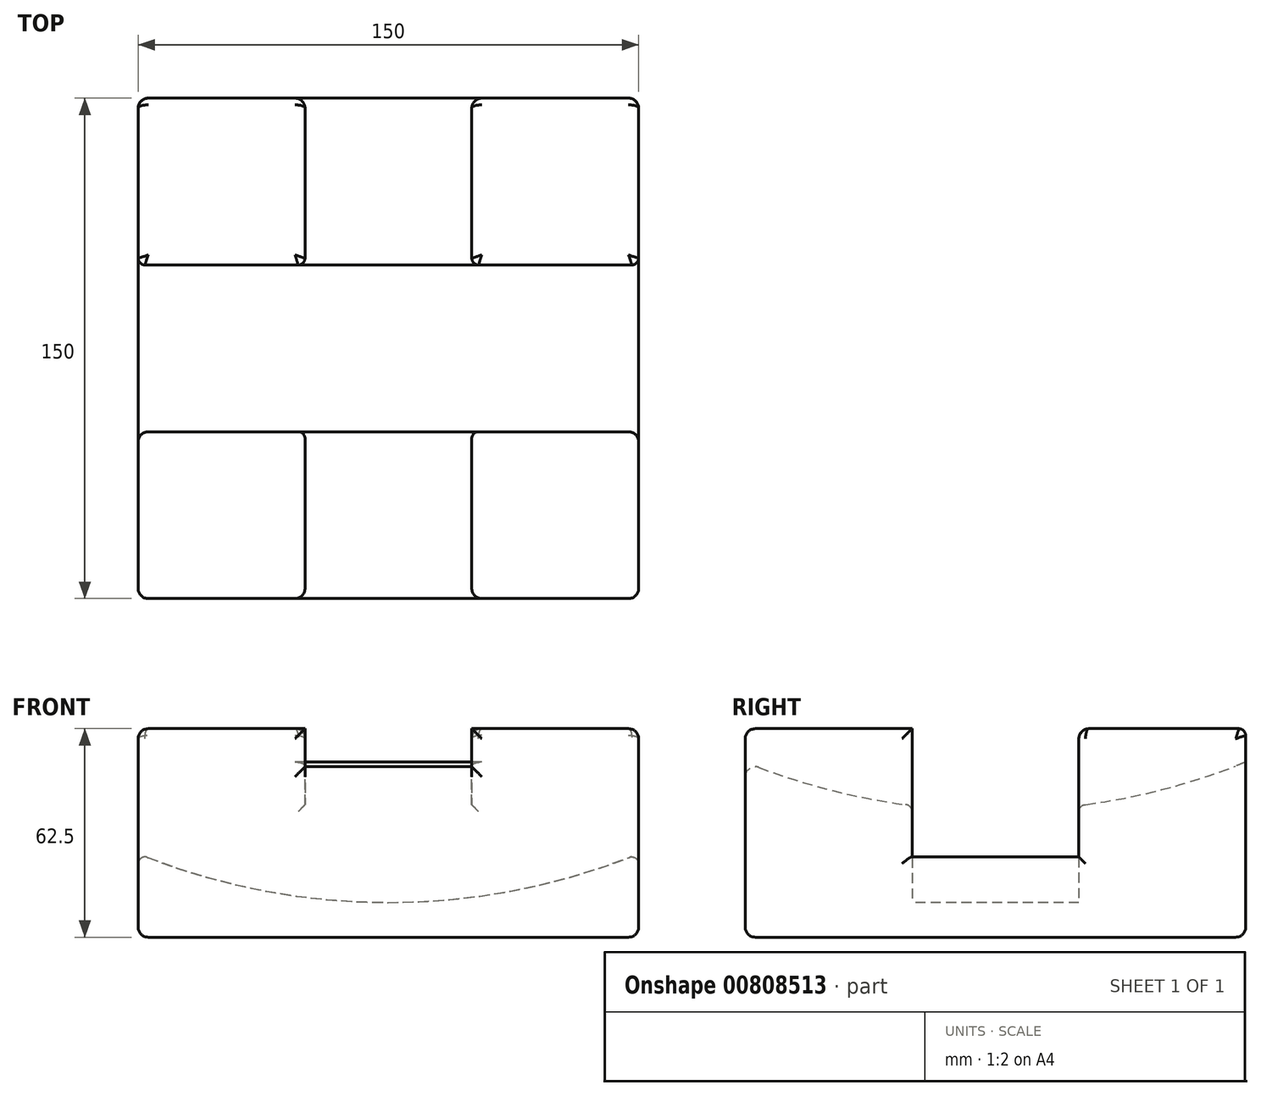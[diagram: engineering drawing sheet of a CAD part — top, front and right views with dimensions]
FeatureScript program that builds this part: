
annotation { "Feature Type Name" : "Feature", "Feature Type Description" : "" }
export const myFeature = defineFeature(function(context is Context, id is Id, definition is map)
    precondition{}
    {
        {
            var Q0;
            Q0=qCreatedBy(makeId("Top.planeOp"),FACE);
            var sketch = newSketch(context, id + "F0", { "sketchPlane" : qUnion([Q0])});
            skLineSegment(sketch, "E0.bottom", {"start": v(75, -75) * mm, "end": v(-75, -75) * mm});
            skLineSegment(sketch, "E0.top", {"start": v(75, 75) * mm, "end": v(-75, 75) * mm});
            skLineSegment(sketch, "E0.left", {"start": v(75, -75) * mm, "end": v(75, 75) * mm});
            skLineSegment(sketch, "E0.right", {"start": v(-75, -75) * mm, "end": v(-75, 75) * mm});
            skPoint(sketch, "E0.middle", {"position": v(0, 0) * mm});
            skSolve(sketch);
        }
        {
            var Q0;
            Q0 = qSketchRegion(id + "F0", true);
            extrude(context, id + "F1", {"entities" : qUnion([Q0]), "depth" : 25 * mm, "offsetDistance" : 25 * mm});
        }
        {
            var Q0;
            Q0=makeQuery(id+"F1.opExtrude","CAP_FACE",FACE,{"disambiguationData":[OSD([sQuery(id+"F0.wireOp",EDGE,"E0.bottom"),sQuery(id+"F0.wireOp",EDGE,"E0.top"),sQuery(id+"F0.wireOp",EDGE,"E0.left"),sQuery(id+"F0.wireOp",EDGE,"E0.right")])],"isStart":false});
            var sketch = newSketch(context, id + "F2", { "sketchPlane" : qUnion([Q0])});
            skLineSegment(sketch, "E1.bottom", {"start": v(-75, 75) * mm, "end": v(75, 75) * mm});
            skLineSegment(sketch, "E1.top", {"start": v(-75, 25) * mm, "end": v(75, 25) * mm});
            skLineSegment(sketch, "E1.left", {"start": v(-75, 75) * mm, "end": v(-75, 25) * mm});
            skLineSegment(sketch, "E1.right", {"start": v(75, 75) * mm, "end": v(75, 25) * mm});
            skLineSegment(sketch, "E2.bottom", {"start": v(75, -75) * mm, "end": v(-75, -75) * mm});
            skLineSegment(sketch, "E2.top", {"start": v(75, -25) * mm, "end": v(-75, -25) * mm});
            skLineSegment(sketch, "E2.left", {"start": v(75, -75) * mm, "end": v(75, -25) * mm});
            skLineSegment(sketch, "E2.right", {"start": v(-75, -75) * mm, "end": v(-75, -25) * mm});
            skSolve(sketch);
        }
        {
            var Q0;
            Q0=qCreatedBy(makeId("Front.planeOp"),FACE);
            var sketch = newSketch(context, id + "F3", { "sketchPlane" : qUnion([Q0])});
            skLineSegment(sketch, "E3.0", {"start": v(-75, 25) * mm, "end": v(-75, 0) * mm, "construction": true});
            skLineSegment(sketch, "E4.0", {"start": v(75, 25) * mm, "end": v(75, 0) * mm, "construction": true});
            skArc(sketch, "E5", {"start": v(-75, 25) * mm, "mid": v(0, 10.4) * mm, "end": v(75, 25) * mm});
            skLineSegment(sketch, "E6", {"start": v(-75, 25) * mm, "end": v(75, 25) * mm});
            skSolve(sketch);
        }
        {
            var Q0;
            Q0 = qSketchRegion(id + "F3", true);
            extrude(context, id + "F4", {"entities" : qUnion([Q0]), "operationType" : NewBodyOperationType.REMOVE, "oppositeDirection" : true, "depth" : 50 * mm, "offsetDistance" : 25 * mm, "symmetric" : true});
        }
        {
            var Q0;
            Q0 = qSketchRegion(id + "F2", true);
            extrude(context, id + "F5", {"entities" : qUnion([Q0]), "operationType" : NewBodyOperationType.ADD, "depth" : 37.5 * mm, "offsetDistance" : 25 * mm});
        }
        {
            var Q0;
            Q0=qCreatedBy(makeId("Right.planeOp"),FACE);
            var sketch = newSketch(context, id + "F6", { "sketchPlane" : qUnion([Q0])});
            skLineSegment(sketch, "E7.0", {"start": v(75, 62.5) * mm, "end": v(75, 0) * mm, "construction": true});
            skLineSegment(sketch, "E8.0", {"start": v(25, 62.5) * mm, "end": v(75, 62.5) * mm, "construction": true});
            skLineSegment(sketch, "E9.0", {"start": v(-75, 10.03) * mm, "end": v(-75, 0) * mm, "construction": true});
            skLineSegment(sketch, "E10", {"start": v(75, 62.5) * mm, "end": v(75, 10.03) * mm});
            skLineSegment(sketch, "E11", {"start": v(75, 52.5) * mm, "end": v(-75, 52.5) * mm, "construction": true});
            skArc(sketch, "E12", {"start": v(-75, 52.5) * mm, "mid": v(0, 37.9) * mm, "end": v(75, 52.5) * mm});
            skLineSegment(sketch, "E13", {"start": v(75, 52.5) * mm, "end": v(75, 62.5) * mm});
            skLineSegment(sketch, "E14", {"start": v(75, 62.5) * mm, "end": v(-75, 62.5) * mm});
            skLineSegment(sketch, "E15", {"start": v(-75, 62.5) * mm, "end": v(-75, 52.5) * mm});
            skSolve(sketch);
        }
        {
            var Q0;
            Q0 = qSketchRegion(id + "F6", true);
            extrude(context, id + "F7", {"entities" : qUnion([Q0]), "operationType" : NewBodyOperationType.REMOVE, "depth" : 50 * mm, "offsetDistance" : 25 * mm, "symmetric" : true});
        }
        {
            var Q0;
            {var subQ0=sQuery(id+"F2.wireOp",EDGE,"E1.bottom");Q0=makeQuery(id+"F7.boolean.opBoolean","SPLIT",EDGE,{"disambiguationData":[TD([makeQuery(id+"F1.opExtrude","SWEPT_FACE",FACE,{"disambiguationData":[OSD([sQuery(id+"F0.wireOp",EDGE,"E0.left")])]})])],"derivedFrom":makeQuery(id+"F5.opExtrude","CAP_EDGE",EDGE,{"disambiguationData":[OSD([subQ0])],"isStart":false})});}
            var Q1;
            {var subQ1=sQuery(id+"F2.wireOp",EDGE,"E1.bottom");Q1=makeQuery(id+"F7.boolean.opBoolean","SPLIT",EDGE,{"disambiguationData":[TD([makeQuery(id+"F1.opExtrude","SWEPT_FACE",FACE,{"disambiguationData":[OSD([sQuery(id+"F0.wireOp",EDGE,"E0.right")])]})])],"derivedFrom":makeQuery(id+"F5.opExtrude","CAP_EDGE",EDGE,{"disambiguationData":[OSD([subQ1])],"isStart":false})});}
            var Q2;
            {var subQ0=sQuery(id+"F3.wireOp",EDGE,"E6");var subQ1=sQuery(id+"F3.wireOp",EDGE,"E5");Q2=makeQuery(id+"F4.boolean.opBoolean","MERGE",EDGE,{"derivedFrom":[makeQuery(id+"F1.opExtrude","CAP_EDGE",EDGE,{"disambiguationData":[OSD([sQuery(id+"F0.wireOp",EDGE,"E0.left")])],"isStart":false}),makeQuery(id+"F4.opExtrude","SWEPT_EDGE",EDGE,{"disambiguationData":[OSD([subQ1,subQ0]),TDD([makeQuery(id+"F3.imprint","INTERSECT",VERTEX,{"disambiguationData":[OD(1.0)],"derivedFrom":[subQ1,subQ0]})])]})]});}
            var Q3;
            {var subQ0=sQuery(id+"F3.wireOp",EDGE,"E6");var subQ1=sQuery(id+"F3.wireOp",EDGE,"E5");Q3=makeQuery(id+"F4.boolean.opBoolean","MERGE",EDGE,{"derivedFrom":[makeQuery(id+"F1.opExtrude","CAP_EDGE",EDGE,{"disambiguationData":[OSD([sQuery(id+"F0.wireOp",EDGE,"E0.right")])],"isStart":false}),makeQuery(id+"F4.opExtrude","SWEPT_EDGE",EDGE,{"disambiguationData":[OSD([subQ1,subQ0]),TDD([makeQuery(id+"F3.imprint","INTERSECT",VERTEX,{"disambiguationData":[OD(0.0)],"derivedFrom":[subQ1,subQ0]})])]})]});}
            var Q4;
            Q4=makeQuery(id+"F5.opExtrude","SWEPT_EDGE",EDGE,{"disambiguationData":[OSD([sQuery(id+"F0.wireOp",EDGE,"E0.right"),sQuery(id+"F2.wireOp",EDGE,"E1.top"),sQuery(id+"F2.wireOp",EDGE,"E1.left")])]});
            var Q5;
            Q5=makeQuery(id+"F5.opExtrude","SWEPT_EDGE",EDGE,{"disambiguationData":[OSD([sQuery(id+"F0.wireOp",EDGE,"E0.left"),sQuery(id+"F2.wireOp",EDGE,"E1.top"),sQuery(id+"F2.wireOp",EDGE,"E1.right")])]});
            var Q6;
            Q6=makeQuery(id+"F7.boolean.opBoolean","COPY",EDGE,{"derivedFrom":makeQuery(id+"F7.opExtrude","SWEPT_EDGE",EDGE,{"disambiguationData":[OSD([sQuery(id+"F6.wireOp",EDGE,"E12"),sQuery(id+"F6.wireOp",EDGE,"E15")])]})});
            var Q7;
            Q7=makeQuery(id+"F7.boolean.opBoolean","INTERSECT",EDGE,{"derivedFrom":[makeQuery(id+"F5.boolean.opBoolean","MERGE",FACE,{"derivedFrom":[makeQuery(id+"F4.boolean.opBoolean","COPY",FACE,{"derivedFrom":makeQuery(id+"F4.opExtrude","CAP_FACE",FACE,{"disambiguationData":[OSD([sQuery(id+"F3.wireOp",EDGE,"E5"),sQuery(id+"F3.wireOp",EDGE,"E6")])],"isStart":true})}),makeQuery(id+"F5.opExtrude","SWEPT_FACE",FACE,{"disambiguationData":[OSD([sQuery(id+"F2.wireOp",EDGE,"E2.top")])]})]}),makeQuery(id+"F7.opExtrude","SWEPT_FACE",FACE,{"disambiguationData":[OSD([sQuery(id+"F6.wireOp",EDGE,"E12")])]})]});
            var Q8;
            Q8=makeQuery(id+"F7.boolean.opBoolean","INTERSECT",EDGE,{"derivedFrom":[makeQuery(id+"F5.boolean.opBoolean","MERGE",FACE,{"derivedFrom":[makeQuery(id+"F4.boolean.opBoolean","COPY",FACE,{"derivedFrom":makeQuery(id+"F4.opExtrude","CAP_FACE",FACE,{"disambiguationData":[OSD([sQuery(id+"F3.wireOp",EDGE,"E5"),sQuery(id+"F3.wireOp",EDGE,"E6")])],"isStart":true})}),makeQuery(id+"F5.opExtrude","SWEPT_FACE",FACE,{"disambiguationData":[OSD([sQuery(id+"F2.wireOp",EDGE,"E2.top")])]})]}),makeQuery(id+"F7.opExtrude","CAP_FACE",FACE,{"disambiguationData":[OSD([sQuery(id+"F6.wireOp",EDGE,"E12"),sQuery(id+"F6.wireOp",EDGE,"E13"),sQuery(id+"F6.wireOp",EDGE,"E14"),sQuery(id+"F6.wireOp",EDGE,"E15")])],"isStart":false})]});
            var Q9;
            Q9=makeQuery(id+"F7.boolean.opBoolean","INTERSECT",EDGE,{"derivedFrom":[makeQuery(id+"F5.boolean.opBoolean","MERGE",FACE,{"derivedFrom":[makeQuery(id+"F4.boolean.opBoolean","COPY",FACE,{"derivedFrom":makeQuery(id+"F4.opExtrude","CAP_FACE",FACE,{"disambiguationData":[OSD([sQuery(id+"F3.wireOp",EDGE,"E5"),sQuery(id+"F3.wireOp",EDGE,"E6")])],"isStart":false})}),makeQuery(id+"F5.opExtrude","SWEPT_FACE",FACE,{"disambiguationData":[OSD([sQuery(id+"F2.wireOp",EDGE,"E1.top")])]})]}),makeQuery(id+"F7.opExtrude","CAP_FACE",FACE,{"disambiguationData":[OSD([sQuery(id+"F6.wireOp",EDGE,"E12"),sQuery(id+"F6.wireOp",EDGE,"E13"),sQuery(id+"F6.wireOp",EDGE,"E14"),sQuery(id+"F6.wireOp",EDGE,"E15")])],"isStart":false})]});
            var Q10;
            Q10=makeQuery(id+"F7.boolean.opBoolean","COPY",EDGE,{"derivedFrom":makeQuery(id+"F7.opExtrude","SWEPT_EDGE",EDGE,{"disambiguationData":[OSD([sQuery(id+"F6.wireOp",EDGE,"E12"),sQuery(id+"F6.wireOp",EDGE,"E13")])]})});
            var Q11;
            Q11=makeQuery(id+"F7.boolean.opBoolean","INTERSECT",EDGE,{"derivedFrom":[makeQuery(id+"F5.boolean.opBoolean","MERGE",FACE,{"derivedFrom":[makeQuery(id+"F4.boolean.opBoolean","COPY",FACE,{"derivedFrom":makeQuery(id+"F4.opExtrude","CAP_FACE",FACE,{"disambiguationData":[OSD([sQuery(id+"F3.wireOp",EDGE,"E5"),sQuery(id+"F3.wireOp",EDGE,"E6")])],"isStart":false})}),makeQuery(id+"F5.opExtrude","SWEPT_FACE",FACE,{"disambiguationData":[OSD([sQuery(id+"F2.wireOp",EDGE,"E1.top")])]})]}),makeQuery(id+"F7.opExtrude","SWEPT_FACE",FACE,{"disambiguationData":[OSD([sQuery(id+"F6.wireOp",EDGE,"E12")])]})]});
            var Q12;
            Q12=makeQuery(id+"F7.boolean.opBoolean","COPY",EDGE,{"derivedFrom":makeQuery(id+"F7.opExtrude","CAP_EDGE",EDGE,{"disambiguationData":[OSD([sQuery(id+"F6.wireOp",EDGE,"E15")])],"isStart":false})});
            var Q13;
            Q13=makeQuery(id+"F7.boolean.opBoolean","COPY",EDGE,{"derivedFrom":makeQuery(id+"F7.opExtrude","CAP_EDGE",EDGE,{"disambiguationData":[OSD([sQuery(id+"F6.wireOp",EDGE,"E15")])],"isStart":true})});
            var Q14;
            Q14=makeQuery(id+"F7.boolean.opBoolean","INTERSECT",EDGE,{"derivedFrom":[makeQuery(id+"F5.boolean.opBoolean","MERGE",FACE,{"derivedFrom":[makeQuery(id+"F4.boolean.opBoolean","COPY",FACE,{"derivedFrom":makeQuery(id+"F4.opExtrude","CAP_FACE",FACE,{"disambiguationData":[OSD([sQuery(id+"F3.wireOp",EDGE,"E5"),sQuery(id+"F3.wireOp",EDGE,"E6")])],"isStart":false})}),makeQuery(id+"F5.opExtrude","SWEPT_FACE",FACE,{"disambiguationData":[OSD([sQuery(id+"F2.wireOp",EDGE,"E1.top")])]})]}),makeQuery(id+"F7.opExtrude","CAP_FACE",FACE,{"disambiguationData":[OSD([sQuery(id+"F6.wireOp",EDGE,"E12"),sQuery(id+"F6.wireOp",EDGE,"E13"),sQuery(id+"F6.wireOp",EDGE,"E14"),sQuery(id+"F6.wireOp",EDGE,"E15")])],"isStart":true})]});
            var Q15;
            Q15=makeQuery(id+"F7.boolean.opBoolean","COPY",EDGE,{"derivedFrom":makeQuery(id+"F7.opExtrude","CAP_EDGE",EDGE,{"disambiguationData":[OSD([sQuery(id+"F6.wireOp",EDGE,"E13")])],"isStart":false})});
            var Q16;
            Q16=makeQuery(id+"F7.boolean.opBoolean","COPY",EDGE,{"derivedFrom":makeQuery(id+"F7.opExtrude","CAP_EDGE",EDGE,{"disambiguationData":[OSD([sQuery(id+"F6.wireOp",EDGE,"E13")])],"isStart":true})});
            var Q17;
            Q17=makeQuery(id+"F7.boolean.opBoolean","INTERSECT",EDGE,{"derivedFrom":[makeQuery(id+"F5.boolean.opBoolean","MERGE",FACE,{"derivedFrom":[makeQuery(id+"F4.boolean.opBoolean","COPY",FACE,{"derivedFrom":makeQuery(id+"F4.opExtrude","CAP_FACE",FACE,{"disambiguationData":[OSD([sQuery(id+"F3.wireOp",EDGE,"E5"),sQuery(id+"F3.wireOp",EDGE,"E6")])],"isStart":true})}),makeQuery(id+"F5.opExtrude","SWEPT_FACE",FACE,{"disambiguationData":[OSD([sQuery(id+"F2.wireOp",EDGE,"E2.top")])]})]}),makeQuery(id+"F7.opExtrude","CAP_FACE",FACE,{"disambiguationData":[OSD([sQuery(id+"F6.wireOp",EDGE,"E12"),sQuery(id+"F6.wireOp",EDGE,"E13"),sQuery(id+"F6.wireOp",EDGE,"E14"),sQuery(id+"F6.wireOp",EDGE,"E15")])],"isStart":true})]});
            fillet(context, id + "F8", {"entities" : qUnion([Q0, Q1, Q2, Q3, Q4, Q5, Q6, Q7, Q8, Q9, Q10, Q11, Q12, Q13, Q14, Q15, Q16, Q17]), "radius" : 2 * mm, "tangentPropagation" : true, "allowEdgeOverflow" : false});
        }
        {
            var Q0;
            Q0=makeQuery(id+"F1.opExtrude","CAP_FACE",FACE,{"disambiguationData":[OSD([sQuery(id+"F0.wireOp",EDGE,"E0.bottom"),sQuery(id+"F0.wireOp",EDGE,"E0.top"),sQuery(id+"F0.wireOp",EDGE,"E0.left"),sQuery(id+"F0.wireOp",EDGE,"E0.right")])],"isStart":true});
            var Q1;
            {var subQ1=sQuery(id+"F2.wireOp",EDGE,"E1.top");Q1=makeQuery(id+"F7.boolean.opBoolean","SPLIT",EDGE,{"disambiguationData":[TD([makeQuery(id+"F1.opExtrude","SWEPT_FACE",FACE,{"disambiguationData":[OSD([sQuery(id+"F0.wireOp",EDGE,"E0.right")])]})])],"derivedFrom":makeQuery(id+"F5.opExtrude","CAP_EDGE",EDGE,{"disambiguationData":[OSD([subQ1])],"isStart":false})});}
            var Q2;
            {var subQ1=sQuery(id+"F2.wireOp",EDGE,"E1.top");Q2=makeQuery(id+"F7.boolean.opBoolean","SPLIT",EDGE,{"disambiguationData":[TD([makeQuery(id+"F1.opExtrude","SWEPT_FACE",FACE,{"disambiguationData":[OSD([sQuery(id+"F0.wireOp",EDGE,"E0.left")])]})])],"derivedFrom":makeQuery(id+"F5.opExtrude","CAP_EDGE",EDGE,{"disambiguationData":[OSD([subQ1])],"isStart":false})});}
            var Q3;
            {var subQ1=sQuery(id+"Fx0xP4mrSlEMWPA_1.wireOp",EDGE,"fe122eca-1263-42cf-97f3-6efdb6687c8c.0");Q3=makeQuery(id+"F7.boolean.opBoolean","SPLIT",EDGE,{"disambiguationData":[TD([makeQuery(id+"F1.opExtrude","SWEPT_FACE",FACE,{"disambiguationData":[OSD([sQuery(id+"F0.wireOp",EDGE,"E0.left")])]})])],"derivedFrom":makeQuery(id+"FigQ51f6E0wQWOO_1.opExtrude","CAP_EDGE",EDGE,{"disambiguationData":[OSD([subQ1])],"isStart":false})});}
            var Q4;
            {var subQ0=sQuery(id+"Fx0xP4mrSlEMWPA_1.wireOp",EDGE,"fe122eca-1263-42cf-97f3-6efdb6687c8c.0");Q4=makeQuery(id+"F7.boolean.opBoolean","SPLIT",EDGE,{"disambiguationData":[TD([makeQuery(id+"F1.opExtrude","SWEPT_FACE",FACE,{"disambiguationData":[OSD([sQuery(id+"F0.wireOp",EDGE,"E0.right")])]})])],"derivedFrom":makeQuery(id+"FigQ51f6E0wQWOO_1.opExtrude","CAP_EDGE",EDGE,{"disambiguationData":[OSD([subQ0])],"isStart":false})});}
            var Q5;
            {var subQ0=sQuery(id+"F2.wireOp",EDGE,"E1.bottom");Q5=makeQuery(id+"F7.boolean.opBoolean","SPLIT",EDGE,{"disambiguationData":[TD([makeQuery(id+"F1.opExtrude","SWEPT_FACE",FACE,{"disambiguationData":[OSD([sQuery(id+"F0.wireOp",EDGE,"E0.right")])]})])],"derivedFrom":makeQuery(id+"F5.opExtrude","CAP_EDGE",EDGE,{"disambiguationData":[OSD([subQ0])],"isStart":false})});}
            var Q6;
            {var subQ0=sQuery(id+"F2.wireOp",EDGE,"E1.bottom");Q6=makeQuery(id+"F7.boolean.opBoolean","SPLIT",EDGE,{"disambiguationData":[TD([makeQuery(id+"F1.opExtrude","SWEPT_FACE",FACE,{"disambiguationData":[OSD([sQuery(id+"F0.wireOp",EDGE,"E0.left")])]})])],"derivedFrom":makeQuery(id+"F5.opExtrude","CAP_EDGE",EDGE,{"disambiguationData":[OSD([subQ0])],"isStart":false})});}
            var Q7;
            {var subQ1=sQuery(id+"Fx0xP4mrSlEMWPA_1.wireOp",EDGE,"019585a6-d1d0-47e1-8fcd-0abe2f224d58.0");Q7=makeQuery(id+"F7.boolean.opBoolean","SPLIT",EDGE,{"disambiguationData":[TD([makeQuery(id+"F1.opExtrude","SWEPT_FACE",FACE,{"disambiguationData":[OSD([sQuery(id+"F0.wireOp",EDGE,"E0.left")])]})])],"derivedFrom":makeQuery(id+"FigQ51f6E0wQWOO_1.opExtrude","CAP_EDGE",EDGE,{"disambiguationData":[OSD([subQ1])],"isStart":false})});}
            var Q8;
            {var subQ0=sQuery(id+"Fx0xP4mrSlEMWPA_1.wireOp",EDGE,"019585a6-d1d0-47e1-8fcd-0abe2f224d58.0");Q8=makeQuery(id+"F7.boolean.opBoolean","SPLIT",EDGE,{"disambiguationData":[TD([makeQuery(id+"F1.opExtrude","SWEPT_FACE",FACE,{"disambiguationData":[OSD([sQuery(id+"F0.wireOp",EDGE,"E0.right")])]})])],"derivedFrom":makeQuery(id+"FigQ51f6E0wQWOO_1.opExtrude","CAP_EDGE",EDGE,{"disambiguationData":[OSD([subQ0])],"isStart":false})});}
            var Q9;
            Q9=makeQuery(id+"F5.boolean.opBoolean","MERGE",EDGE,{"derivedFrom":[makeQuery(id+"F1.opExtrude","SWEPT_EDGE",EDGE,{"disambiguationData":[OSD([sQuery(id+"F0.wireOp",EDGE,"E0.top"),sQuery(id+"F0.wireOp",EDGE,"E0.right")])]}),makeQuery(id+"F5.opExtrude","SWEPT_EDGE",EDGE,{"disambiguationData":[OSD([sQuery(id+"F2.wireOp",EDGE,"E1.bottom"),sQuery(id+"F2.wireOp",EDGE,"E1.left")])]})]});
            var Q10;
            Q10=makeQuery(id+"FigQ51f6E0wQWOO_1.boolean.opBoolean","MERGE",EDGE,{"derivedFrom":[makeQuery(id+"F1.opExtrude","SWEPT_EDGE",EDGE,{"disambiguationData":[OSD([sQuery(id+"F0.wireOp",EDGE,"E0.bottom"),sQuery(id+"F0.wireOp",EDGE,"E0.right")])]}),makeQuery(id+"FigQ51f6E0wQWOO_1.opExtrude","SWEPT_EDGE",EDGE,{"disambiguationData":[OSD([sQuery(id+"Fx0xP4mrSlEMWPA_1.wireOp",EDGE,"f2ef4f2c-1ebd-42c5-9d36-b560bfb08982.0"),sQuery(id+"Fx0xP4mrSlEMWPA_1.wireOp",EDGE,"019585a6-d1d0-47e1-8fcd-0abe2f224d58.0")])]})]});
            var Q11;
            Q11=makeQuery(id+"FigQ51f6E0wQWOO_1.boolean.opBoolean","MERGE",EDGE,{"derivedFrom":[makeQuery(id+"F1.opExtrude","SWEPT_EDGE",EDGE,{"disambiguationData":[OSD([sQuery(id+"F0.wireOp",EDGE,"E0.bottom"),sQuery(id+"F0.wireOp",EDGE,"E0.left")])]}),makeQuery(id+"FigQ51f6E0wQWOO_1.opExtrude","SWEPT_EDGE",EDGE,{"disambiguationData":[OSD([sQuery(id+"Fx0xP4mrSlEMWPA_1.wireOp",EDGE,"a8fba2bb-0058-453a-8391-7f5e07edb9f2.0"),sQuery(id+"Fx0xP4mrSlEMWPA_1.wireOp",EDGE,"019585a6-d1d0-47e1-8fcd-0abe2f224d58.0")])]})]});
            var Q12;
            Q12=makeQuery(id+"F5.boolean.opBoolean","MERGE",EDGE,{"derivedFrom":[makeQuery(id+"F1.opExtrude","SWEPT_EDGE",EDGE,{"disambiguationData":[OSD([sQuery(id+"F0.wireOp",EDGE,"E0.top"),sQuery(id+"F0.wireOp",EDGE,"E0.left")])]}),makeQuery(id+"F5.opExtrude","SWEPT_EDGE",EDGE,{"disambiguationData":[OSD([sQuery(id+"F2.wireOp",EDGE,"E1.bottom"),sQuery(id+"F2.wireOp",EDGE,"E1.right")])]})]});
            var Q13;
            Q13=makeQuery(id+"F5.boolean.opBoolean","MERGE",FACE,{"derivedFrom":[makeQuery(id+"F1.opExtrude","SWEPT_FACE",FACE,{"disambiguationData":[OSD([sQuery(id+"F0.wireOp",EDGE,"E0.right")])]}),makeQuery(id+"F5.opExtrude","SWEPT_FACE",FACE,{"disambiguationData":[OSD([sQuery(id+"F2.wireOp",EDGE,"E1.left")])]}),makeQuery(id+"F5.opExtrude","SWEPT_FACE",FACE,{"disambiguationData":[OSD([sQuery(id+"F2.wireOp",EDGE,"E2.right")])]})]});
            var Q14;
            Q14=makeQuery(id+"F5.boolean.opBoolean","MERGE",FACE,{"derivedFrom":[makeQuery(id+"F1.opExtrude","SWEPT_FACE",FACE,{"disambiguationData":[OSD([sQuery(id+"F0.wireOp",EDGE,"E0.bottom")])]}),makeQuery(id+"F5.opExtrude","SWEPT_FACE",FACE,{"disambiguationData":[OSD([sQuery(id+"F2.wireOp",EDGE,"E2.bottom")])]})]});
            var Q15;
            Q15=makeQuery(id+"F5.boolean.opBoolean","MERGE",FACE,{"derivedFrom":[makeQuery(id+"F1.opExtrude","SWEPT_FACE",FACE,{"disambiguationData":[OSD([sQuery(id+"F0.wireOp",EDGE,"E0.left")])]}),makeQuery(id+"F5.opExtrude","SWEPT_FACE",FACE,{"disambiguationData":[OSD([sQuery(id+"F2.wireOp",EDGE,"E1.right")])]}),makeQuery(id+"F5.opExtrude","SWEPT_FACE",FACE,{"disambiguationData":[OSD([sQuery(id+"F2.wireOp",EDGE,"E2.left")])]})]});
            fillet(context, id + "F9", {"entities" : qUnion([Q0, Q1, Q2, Q3, Q4, Q5, Q6, Q7, Q8, Q9, Q10, Q11, Q12, Q13, Q14, Q15]), "radius" : 3 * mm, "tangentPropagation" : true, "allowEdgeOverflow" : false});
        }
    });
